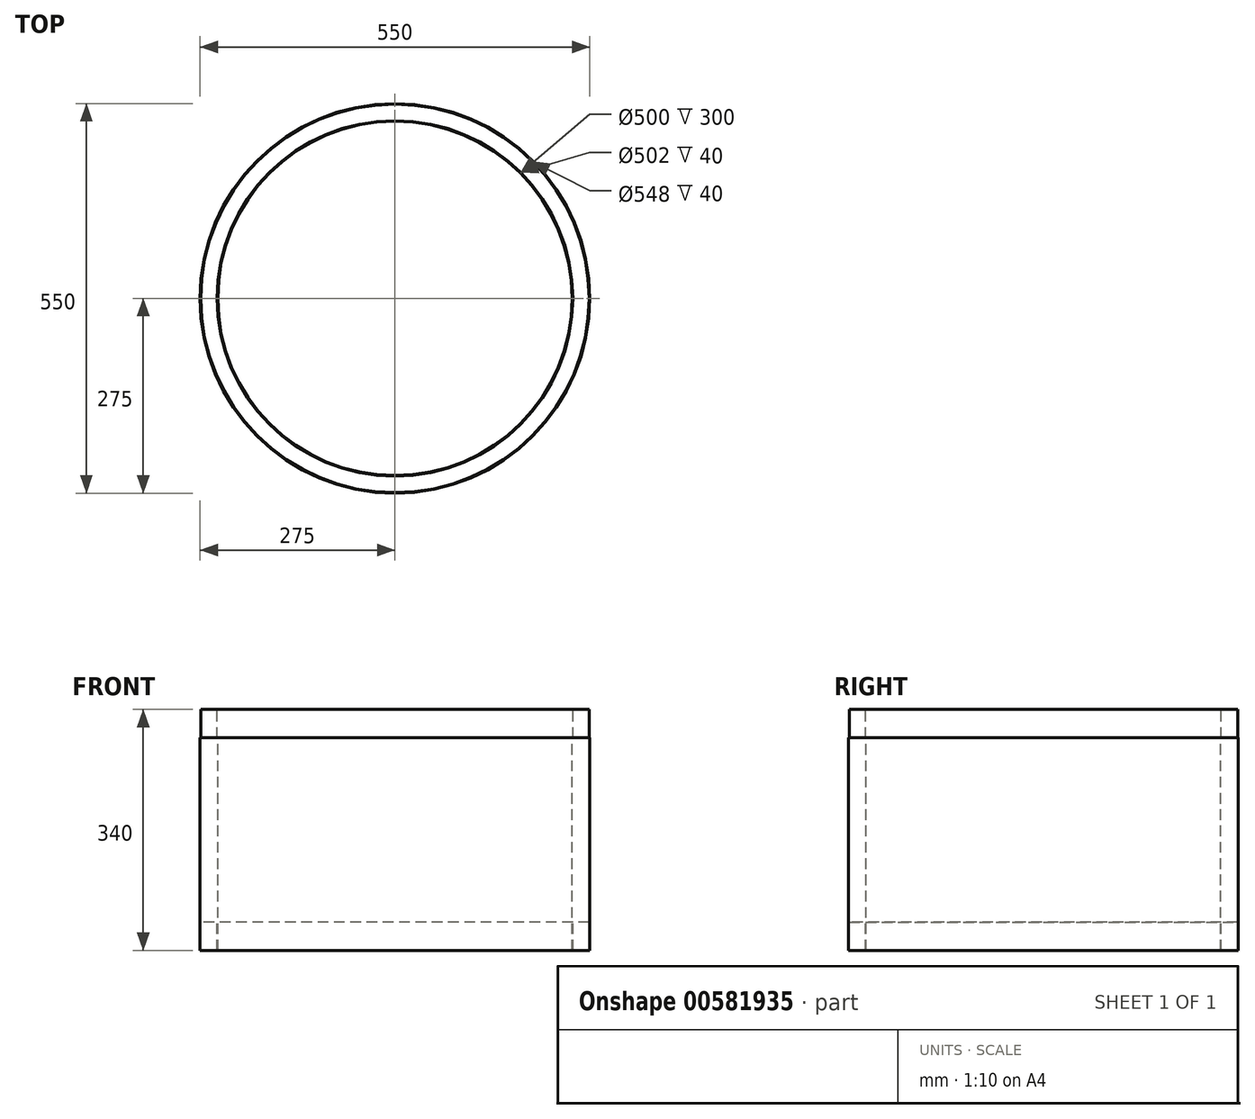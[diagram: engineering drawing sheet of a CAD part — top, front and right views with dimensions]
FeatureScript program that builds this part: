
annotation { "Feature Type Name" : "Feature", "Feature Type Description" : "" }
export const myFeature = defineFeature(function(context is Context, id is Id, definition is map)
    precondition{}
    {
        {
            var Q0;
            Q0=qCreatedBy(makeId("Front.planeOp"),FACE);
            var sketch = newSketch(context, id + "F0", { "sketchPlane" : qUnion([Q0])});
            skLineSegment(sketch, "E0", {"start": v(0, 345.75) * mm, "end": v(0, -558.03) * mm, "construction": true});
            skLineSegment(sketch, "E1", {"start": v(-250, -518.84) * mm, "end": v(-250, -218.84) * mm});
            skLineSegment(sketch, "E2", {"start": v(-250, -218.84) * mm, "end": v(-251, -218.84) * mm});
            skLineSegment(sketch, "E3", {"start": v(-251, -218.84) * mm, "end": v(-251, -178.84) * mm});
            skLineSegment(sketch, "E4", {"start": v(-251, -178.84) * mm, "end": v(-274, -178.84) * mm});
            skLineSegment(sketch, "E5", {"start": v(-274, -178.84) * mm, "end": v(-274, -218.84) * mm});
            skLineSegment(sketch, "E6", {"start": v(-274, -218.84) * mm, "end": v(-275, -218.84) * mm});
            skLineSegment(sketch, "E7", {"start": v(-275, -218.84) * mm, "end": v(-275, -518.84) * mm});
            skLineSegment(sketch, "E8", {"start": v(-275, -518.84) * mm, "end": v(-274, -518.84) * mm});
            skLineSegment(sketch, "E9", {"start": v(-274, -518.84) * mm, "end": v(-274, -478.84) * mm});
            skLineSegment(sketch, "E10", {"start": v(-274, -478.84) * mm, "end": v(-251, -478.84) * mm});
            skLineSegment(sketch, "E11", {"start": v(-251, -478.84) * mm, "end": v(-251, -518.84) * mm});
            skLineSegment(sketch, "E12", {"start": v(-251, -518.84) * mm, "end": v(-250, -518.84) * mm});
            skSolve(sketch);
        }
        {
            var Q0;
            Q0=qSketchRegion(id+"F0",true);
            var Q1;
            Q1=sQuery(id+"F0.wireOp",EDGE,"E0");
            revolve(context, id + "F1", {"entities" : qUnion([Q0]), "axis" : qUnion([Q1]), "revolveType" : RevolveType.FULL});
        }
    });
